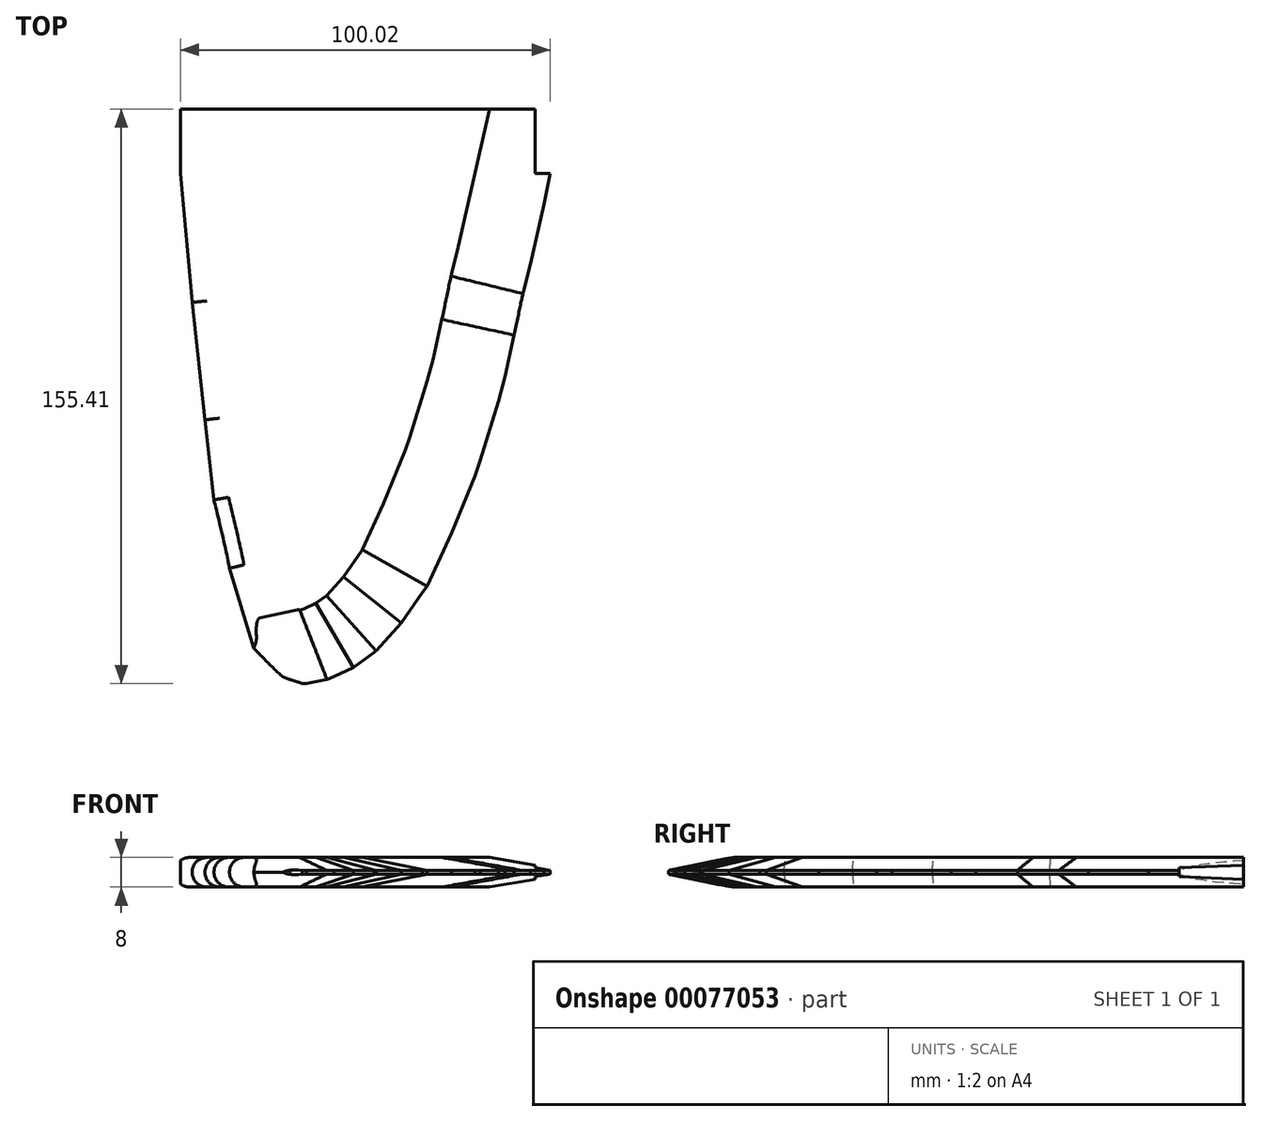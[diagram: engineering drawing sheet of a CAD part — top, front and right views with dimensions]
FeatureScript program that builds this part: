
annotation { "Feature Type Name" : "Feature", "Feature Type Description" : "" }
export const myFeature = defineFeature(function(context is Context, id is Id, definition is map)
    precondition{}
    {
        {
            var Q0;
            Q0=qCreatedBy(makeId("Top.planeOp"),FACE);
            var sketch = newSketch(context, id + "F0", { "sketchPlane" : qUnion([Q0])});
            skLineSegment(sketch, "E0", {"start": v(-143.06, 60.22) * mm, "end": v(-139.92, 25.33) * mm});
            skLineSegment(sketch, "E1", {"start": v(-139.92, 25.33) * mm, "end": v(-136.43, -6.42) * mm});
            skLineSegment(sketch, "E2", {"start": v(-136.43, -6.42) * mm, "end": v(-133.98, -28.05) * mm});
            skLineSegment(sketch, "E3", {"start": v(-133.98, -28.05) * mm, "end": v(-129.8, -46.54) * mm});
            skLineSegment(sketch, "E4", {"start": v(-129.8, -46.54) * mm, "end": v(-123.17, -68.17) * mm});
            skLineSegment(sketch, "E5", {"start": v(-123.17, -68.17) * mm, "end": v(-116.54, -75.5) * mm});
            skLineSegment(sketch, "E6", {"start": v(-116.54, -75.5) * mm, "end": v(-109.91, -77.94) * mm});
            skLineSegment(sketch, "E7", {"start": v(-109.91, -77.94) * mm, "end": v(-103.28, -76.55) * mm});
            skLineSegment(sketch, "E8", {"start": v(-103.28, -76.55) * mm, "end": v(-96.3, -73.4) * mm});
            skLineSegment(sketch, "E9", {"start": v(-96.3, -73.4) * mm, "end": v(-89.68, -68.52) * mm});
            skLineSegment(sketch, "E10", {"start": v(-89.68, -68.52) * mm, "end": v(-83.05, -61.2) * mm});
            skLineSegment(sketch, "E11", {"start": v(-83.05, -61.2) * mm, "end": v(-76.42, -51.43) * mm});
            skLineSegment(sketch, "E12", {"start": v(-76.42, -51.43) * mm, "end": v(-69.79, -37.12) * mm});
            skLineSegment(sketch, "E13", {"start": v(-69.79, -37.12) * mm, "end": v(-62.81, -20.03) * mm});
            skLineSegment(sketch, "E14", {"start": v(-62.81, -20.03) * mm, "end": v(-56.18, 1.6) * mm});
            skLineSegment(sketch, "E15", {"start": v(-56.18, 1.6) * mm, "end": v(-49.55, 30.91) * mm});
            skLineSegment(sketch, "E16", {"start": v(-49.55, 30.91) * mm, "end": v(-42.92, 60.22) * mm});
            skLineSegment(sketch, "E17", {"start": v(-42.92, 60.22) * mm, "end": v(-47.11, 60.22) * mm});
            skLineSegment(sketch, "E18", {"start": v(-47.11, 60.22) * mm, "end": v(-47.11, 77.66) * mm});
            skLineSegment(sketch, "E19", {"start": v(-47.11, 77.66) * mm, "end": v(-143.06, 77.66) * mm});
            skLineSegment(sketch, "E20", {"start": v(-143.06, 77.66) * mm, "end": v(-143.06, 60.22) * mm});
            skLineSegment(sketch, "E21", {"start": v(-143.08, 77.94) * mm, "end": v(-143.08, 57.6) * mm});
            skLineSegment(sketch, "E22", {"start": v(-143.08, 57.6) * mm, "end": v(-139.68, 22.63) * mm});
            skLineSegment(sketch, "E23", {"start": v(-139.68, 22.63) * mm, "end": v(-136.03, -10.25) * mm});
            skLineSegment(sketch, "E24", {"start": v(-136.03, -10.25) * mm, "end": v(-134.73, -24.08) * mm});
            skLineSegment(sketch, "E25", {"start": v(-134.73, -24.08) * mm, "end": v(-134.07, -28.51) * mm});
            skLineSegment(sketch, "E26", {"start": v(-134.07, -28.51) * mm, "end": v(-129.64, -47.95) * mm});
            skLineSegment(sketch, "E27", {"start": v(-129.64, -47.95) * mm, "end": v(-123.12, -68.44) * mm});
            skLineSegment(sketch, "E28", {"start": v(-123.12, -68.44) * mm, "end": v(-120.25, -72.35) * mm});
            skLineSegment(sketch, "E29", {"start": v(-120.25, -72.35) * mm, "end": v(-116.6, -75.61) * mm});
            skLineSegment(sketch, "E30", {"start": v(-116.6, -75.61) * mm, "end": v(-110.2, -77.7) * mm});
            skLineSegment(sketch, "E31", {"start": v(-110.2, -77.7) * mm, "end": v(-106.8, -77.83) * mm});
            skLineSegment(sketch, "E32", {"start": v(-106.8, -77.83) * mm, "end": v(-103.28, -76.52) * mm});
            skLineSegment(sketch, "E33", {"start": v(-103.28, -76.52) * mm, "end": v(-96.1, -73.4) * mm});
            skLineSegment(sketch, "E34", {"start": v(-96.1, -73.4) * mm, "end": v(-90.1, -68.83) * mm});
            skLineSegment(sketch, "E35", {"start": v(-90.1, -68.83) * mm, "end": v(-83.32, -61.4) * mm});
            skLineSegment(sketch, "E36", {"start": v(-83.32, -61.4) * mm, "end": v(-76.15, -51.08) * mm});
            skLineSegment(sketch, "E37", {"start": v(-76.15, -51.08) * mm, "end": v(-71.32, -40.78) * mm});
            skLineSegment(sketch, "E38", {"start": v(-71.32, -40.78) * mm, "end": v(-66.89, -30.6) * mm});
            skLineSegment(sketch, "E39", {"start": v(-66.89, -30.6) * mm, "end": v(-63.5, -21.73) * mm});
            skLineSegment(sketch, "E40", {"start": v(-63.5, -21.73) * mm, "end": v(-60.62, -13.38) * mm});
            skLineSegment(sketch, "E41", {"start": v(-60.62, -13.38) * mm, "end": v(-57.23, -1.9) * mm});
            skLineSegment(sketch, "E42", {"start": v(-57.23, -1.9) * mm, "end": v(-54.36, 9.06) * mm});
            skLineSegment(sketch, "E43", {"start": v(-54.36, 9.06) * mm, "end": v(-50.45, 27.71) * mm});
            skLineSegment(sketch, "E44", {"start": v(-50.45, 27.71) * mm, "end": v(-46.92, 41.94) * mm});
            skLineSegment(sketch, "E45", {"start": v(-46.92, 41.94) * mm, "end": v(-43.01, 60.33) * mm});
            skLineSegment(sketch, "E46", {"start": v(-43.01, 60.33) * mm, "end": v(-47.06, 60.46) * mm});
            skLineSegment(sketch, "E47", {"start": v(-47.06, 60.46) * mm, "end": v(-47.06, 77.94) * mm});
            skLineSegment(sketch, "E48", {"start": v(-47.06, 77.94) * mm, "end": v(-143.08, 77.94) * mm});
            skFitSpline(sketch, "E49", {"points": [v(-143.06, 60.22) * mm, v(-143.08, 57.6) * mm, v(-139.92, 25.33) * mm, v(-139.68, 22.63) * mm, v(-136.43, -6.42) * mm, v(-136.03, -10.25) * mm, v(-134.73, -24.08) * mm, v(-133.98, -28.05) * mm, v(-129.8, -46.54) * mm, v(-129.64, -47.95) * mm, v(-123.17, -68.17) * mm, v(-120.25, -72.35) * mm, v(-116.54, -75.5) * mm, v(-109.91, -77.94) * mm, v(-106.8, -77.83) * mm, v(-103.28, -76.55) * mm, v(-96.1, -73.4) * mm, v(-90.1, -68.83) * mm, v(-83.32, -61.4) * mm, v(-76.15, -51.08) * mm, v(-71.32, -40.78) * mm, v(-69.79, -37.12) * mm, v(-66.89, -30.6) * mm, v(-63.5, -21.73) * mm, v(-62.81, -20.03) * mm, v(-60.62, -13.38) * mm, v(-57.23, -1.9) * mm, v(-56.18, 1.6) * mm, v(-54.36, 9.06) * mm, v(-50.45, 27.71) * mm, v(-49.55, 30.91) * mm, v(-46.92, 41.94) * mm, v(-42.92, 60.22) * mm], "startDerivative": vector(-10.44, -78.3) * mm, "endDerivative": vector(86.1, 398.54) * mm});
            skSolve(sketch);
        }
        {
            var Q0;
            Q0=makeQuery(id+"F0.imprint","IMPRINT",FACE,{"disambiguationData":[TD([[makeQuery(id+"F0.imprint","IMPRINT",EDGE,{"derivedFrom":sQuery(id+"F0.wireOp",EDGE,"E0")}),1.0]])]});
            extrude(context, id + "F1", {"entities" : qUnion([Q0]), "depth" : 4 * mm});
        }
        {
            var Q0;
            Q0=makeQuery(id+"F1.opExtrude","CAP_EDGE",EDGE,{"disambiguationData":[OSD([sQuery(id+"F0.wireOp",EDGE,"E16")])],"isStart":false});
            var Q1;
            Q1=makeQuery(id+"F1.opExtrude","CAP_EDGE",EDGE,{"disambiguationData":[OSD([sQuery(id+"F0.wireOp",EDGE,"E44")])],"isStart":false});
            var Q2;
            {var subQ0=sQuery(id+"F0.wireOp",EDGE,"E49");var subQ1=sQuery(id+"F0.wireOp",EDGE,"E44");Q2=makeQuery(id+"F1.opExtrude","CAP_EDGE",EDGE,{"disambiguationData":[OSD([subQ0]),TDD([makeQuery(id+"F0.imprint","IMPRINT",EDGE,{"disambiguationData":[TD([[makeQuery(id+"F0.imprint","INTERSECT",VERTEX,{"derivedFrom":[sQuery(id+"F0.wireOp",EDGE,"E15"),subQ0]}),-1.0]])],"derivedFrom":subQ0}),makeQuery(id+"F0.imprint","IMPRINT",EDGE,{"disambiguationData":[TD([[makeQuery(id+"F0.imprint","INTERSECT",VERTEX,{"derivedFrom":[subQ1,subQ0]}),1.0]])],"derivedFrom":subQ0})])],"isStart":false});}
            var Q3;
            Q3=makeQuery(id+"F1.opExtrude","CAP_EDGE",EDGE,{"disambiguationData":[OSD([sQuery(id+"F0.wireOp",EDGE,"E15")])],"isStart":false});
            var Q4;
            Q4=makeQuery(id+"F1.opExtrude","CAP_EDGE",EDGE,{"disambiguationData":[OSD([sQuery(id+"F0.wireOp",EDGE,"E42")])],"isStart":false});
            var Q5;
            Q5=makeQuery(id+"F1.opExtrude","CAP_EDGE",EDGE,{"disambiguationData":[OSD([sQuery(id+"F0.wireOp",EDGE,"E14")])],"isStart":false});
            var Q6;
            Q6=makeQuery(id+"F1.opExtrude","CAP_EDGE",EDGE,{"disambiguationData":[OSD([sQuery(id+"F0.wireOp",EDGE,"E40")])],"isStart":false});
            var Q7;
            Q7=makeQuery(id+"F1.opExtrude","CAP_EDGE",EDGE,{"disambiguationData":[OSD([sQuery(id+"F0.wireOp",EDGE,"E13")])],"isStart":false});
            var Q8;
            Q8=makeQuery(id+"F1.opExtrude","CAP_EDGE",EDGE,{"disambiguationData":[OSD([sQuery(id+"F0.wireOp",EDGE,"E12")])],"isStart":false});
            var Q9;
            Q9=makeQuery(id+"F1.opExtrude","CAP_EDGE",EDGE,{"disambiguationData":[OSD([sQuery(id+"F0.wireOp",EDGE,"E11")])],"isStart":false});
            var Q10;
            Q10=makeQuery(id+"F1.opExtrude","CAP_EDGE",EDGE,{"disambiguationData":[OSD([sQuery(id+"F0.wireOp",EDGE,"E36")])],"isStart":false});
            var Q11;
            Q11=makeQuery(id+"F1.opExtrude","CAP_EDGE",EDGE,{"disambiguationData":[OSD([sQuery(id+"F0.wireOp",EDGE,"E35")])],"isStart":false});
            var Q12;
            Q12=makeQuery(id+"F1.opExtrude","CAP_EDGE",EDGE,{"disambiguationData":[OSD([sQuery(id+"F0.wireOp",EDGE,"E34")])],"isStart":false});
            var Q13;
            Q13=makeQuery(id+"F1.opExtrude","CAP_EDGE",EDGE,{"disambiguationData":[OSD([sQuery(id+"F0.wireOp",EDGE,"E9")])],"isStart":false});
            var Q14;
            Q14=makeQuery(id+"F1.opExtrude","CAP_EDGE",EDGE,{"disambiguationData":[OSD([sQuery(id+"F0.wireOp",EDGE,"E8")])],"isStart":false});
            var Q15;
            Q15=makeQuery(id+"F1.opExtrude","CAP_EDGE",EDGE,{"disambiguationData":[OSD([sQuery(id+"F0.wireOp",EDGE,"E33")])],"isStart":false});
            var Q16;
            Q16=makeQuery(id+"F1.opExtrude","CAP_EDGE",EDGE,{"disambiguationData":[OSD([sQuery(id+"F0.wireOp",EDGE,"E32")])],"isStart":false});
            var Q17;
            Q17=makeQuery(id+"F1.opExtrude","CAP_EDGE",EDGE,{"disambiguationData":[OSD([sQuery(id+"F0.wireOp",EDGE,"E7")])],"isStart":false});
            chamfer(context, id + "F2", {"entities" : qUnion([Q0, Q1, Q2, Q3, Q4, Q5, Q6, Q7, Q8, Q9, Q10, Q11, Q12, Q13, Q14, Q15, Q16, Q17]), "chamferType" : ChamferType.OFFSET_ANGLE, "width" : 20 * mm, "oppositeDirection" : false, "angle" : 10 * degree, "tangentPropagation" : true});
        }
        {
            var Q0;
            Q0=makeQuery(id+"F1.opExtrude","CAP_EDGE",EDGE,{"disambiguationData":[OSD([sQuery(id+"F0.wireOp",EDGE,"E0")])],"isStart":false});
            var Q1;
            Q1=makeQuery(id+"F1.opExtrude","CAP_EDGE",EDGE,{"disambiguationData":[OSD([sQuery(id+"F0.wireOp",EDGE,"E1")])],"isStart":false});
            var Q2;
            {var subQ0=sQuery(id+"F0.wireOp",EDGE,"E49");Q2=makeQuery(id+"F1.opExtrude","CAP_EDGE",EDGE,{"disambiguationData":[OSD([subQ0]),TDD([makeQuery(id+"F0.imprint","IMPRINT",EDGE,{"disambiguationData":[TD([[makeQuery(id+"F0.imprint","INTERSECT",VERTEX,{"derivedFrom":[sQuery(id+"F0.wireOp",EDGE,"E1"),subQ0]}),-1.0]])],"derivedFrom":subQ0})])],"isStart":false});}
            var Q3;
            Q3=makeQuery(id+"F1.opExtrude","CAP_EDGE",EDGE,{"disambiguationData":[OSD([sQuery(id+"F0.wireOp",EDGE,"E2")])],"isStart":false});
            var Q4;
            {var subQ0=sQuery(id+"F0.wireOp",EDGE,"E49");var subQ1=sQuery(id+"F0.wireOp",EDGE,"E3");Q4=makeQuery(id+"F1.opExtrude","CAP_EDGE",EDGE,{"disambiguationData":[OSD([subQ0]),TDD([makeQuery(id+"F0.imprint","IMPRINT",EDGE,{"disambiguationData":[TD([[makeQuery(id+"F0.imprint","INTERSECT",VERTEX,{"derivedFrom":[sQuery(id+"F0.wireOp",EDGE,"E2"),subQ1,subQ0]}),-1.0]])],"derivedFrom":subQ0})])],"isStart":false});}
            var Q5;
            Q5=makeQuery(id+"F1.opExtrude","CAP_EDGE",EDGE,{"disambiguationData":[OSD([sQuery(id+"F0.wireOp",EDGE,"E4")])],"isStart":false});
            fillet(context, id + "F3", {"entities" : qUnion([Q0, Q1, Q2, Q3, Q4, Q5]), "radius" : 4 * mm, "tangentPropagation" : true, "allowEdgeOverflow" : false});
        }
        {
            var Q0;
            Q0=makeQuery(id+"F1.opExtrude","SWEPT_BODY",BODY,{"disambiguationData":[OSD([sQuery(id+"F0.wireOp",EDGE,"E0"),sQuery(id+"F0.wireOp",EDGE,"E1"),sQuery(id+"F0.wireOp",EDGE,"E2"),sQuery(id+"F0.wireOp",EDGE,"E4"),sQuery(id+"F0.wireOp",EDGE,"E5"),sQuery(id+"F0.wireOp",EDGE,"E6"),sQuery(id+"F0.wireOp",EDGE,"E7"),sQuery(id+"F0.wireOp",EDGE,"E8"),sQuery(id+"F0.wireOp",EDGE,"E9"),sQuery(id+"F0.wireOp",EDGE,"E11"),sQuery(id+"F0.wireOp",EDGE,"E12"),sQuery(id+"F0.wireOp",EDGE,"E13"),sQuery(id+"F0.wireOp",EDGE,"E14"),sQuery(id+"F0.wireOp",EDGE,"E15"),sQuery(id+"F0.wireOp",EDGE,"E16"),sQuery(id+"F0.wireOp",EDGE,"E17"),sQuery(id+"F0.wireOp",EDGE,"E18"),sQuery(id+"F0.wireOp",EDGE,"E19"),sQuery(id+"F0.wireOp",EDGE,"E20"),sQuery(id+"F0.wireOp",EDGE,"E30"),sQuery(id+"F0.wireOp",EDGE,"E31"),sQuery(id+"F0.wireOp",EDGE,"E32"),sQuery(id+"F0.wireOp",EDGE,"E33"),sQuery(id+"F0.wireOp",EDGE,"E34"),sQuery(id+"F0.wireOp",EDGE,"E35"),sQuery(id+"F0.wireOp",EDGE,"E36"),sQuery(id+"F0.wireOp",EDGE,"E40"),sQuery(id+"F0.wireOp",EDGE,"E42"),sQuery(id+"F0.wireOp",EDGE,"E44"),sQuery(id+"F0.wireOp",EDGE,"E45"),sQuery(id+"F0.wireOp",EDGE,"E49")])]});
            var Q1;
            Q1=qCreatedBy(makeId("Top.planeOp"),FACE);
            mirror(context, id + "F4", {"operationType" : NewBodyOperationType.ADD, "entities" : qUnion([Q0]), "mirrorPlane" : qUnion([Q1])});
        }
        {
            var Q0;
            Q0=makeQuery(id+"F4.opPattern","COPY",EDGE,{"derivedFrom":makeQuery(id+"F2.opChamfer","BLEND_EDGE",EDGE,{"blendedFrom":[makeQuery(id+"F1.opExtrude","CAP_EDGE",EDGE,{"disambiguationData":[OSD([sQuery(id+"F0.wireOp",EDGE,"E7")])],"isStart":false}),makeQuery(id+"F1.opExtrude","SWEPT_FACE",FACE,{"disambiguationData":[OSD([sQuery(id+"F0.wireOp",EDGE,"E5")])]})],"blendedInto":[makeQuery(id+"F1.opExtrude","SWEPT_FACE",FACE,{"disambiguationData":[OSD([sQuery(id+"F0.wireOp",EDGE,"E5")])]})]}),"instanceName":"1"});
            var Q1;
            Q1=makeQuery(id+"F2.opChamfer","BLEND_EDGE",EDGE,{"blendedFrom":[makeQuery(id+"F1.opExtrude","CAP_EDGE",EDGE,{"disambiguationData":[OSD([sQuery(id+"F0.wireOp",EDGE,"E7")])],"isStart":false}),makeQuery(id+"F1.opExtrude","SWEPT_FACE",FACE,{"disambiguationData":[OSD([sQuery(id+"F0.wireOp",EDGE,"E5")])]})],"blendedInto":[makeQuery(id+"F1.opExtrude","SWEPT_FACE",FACE,{"disambiguationData":[OSD([sQuery(id+"F0.wireOp",EDGE,"E5")])]})]});
            fillet(context, id + "F5", {"entities" : qUnion([Q0, Q1]), "radius" : 3 * mm, "tangentPropagation" : true, "allowEdgeOverflow" : false});
        }
    });
